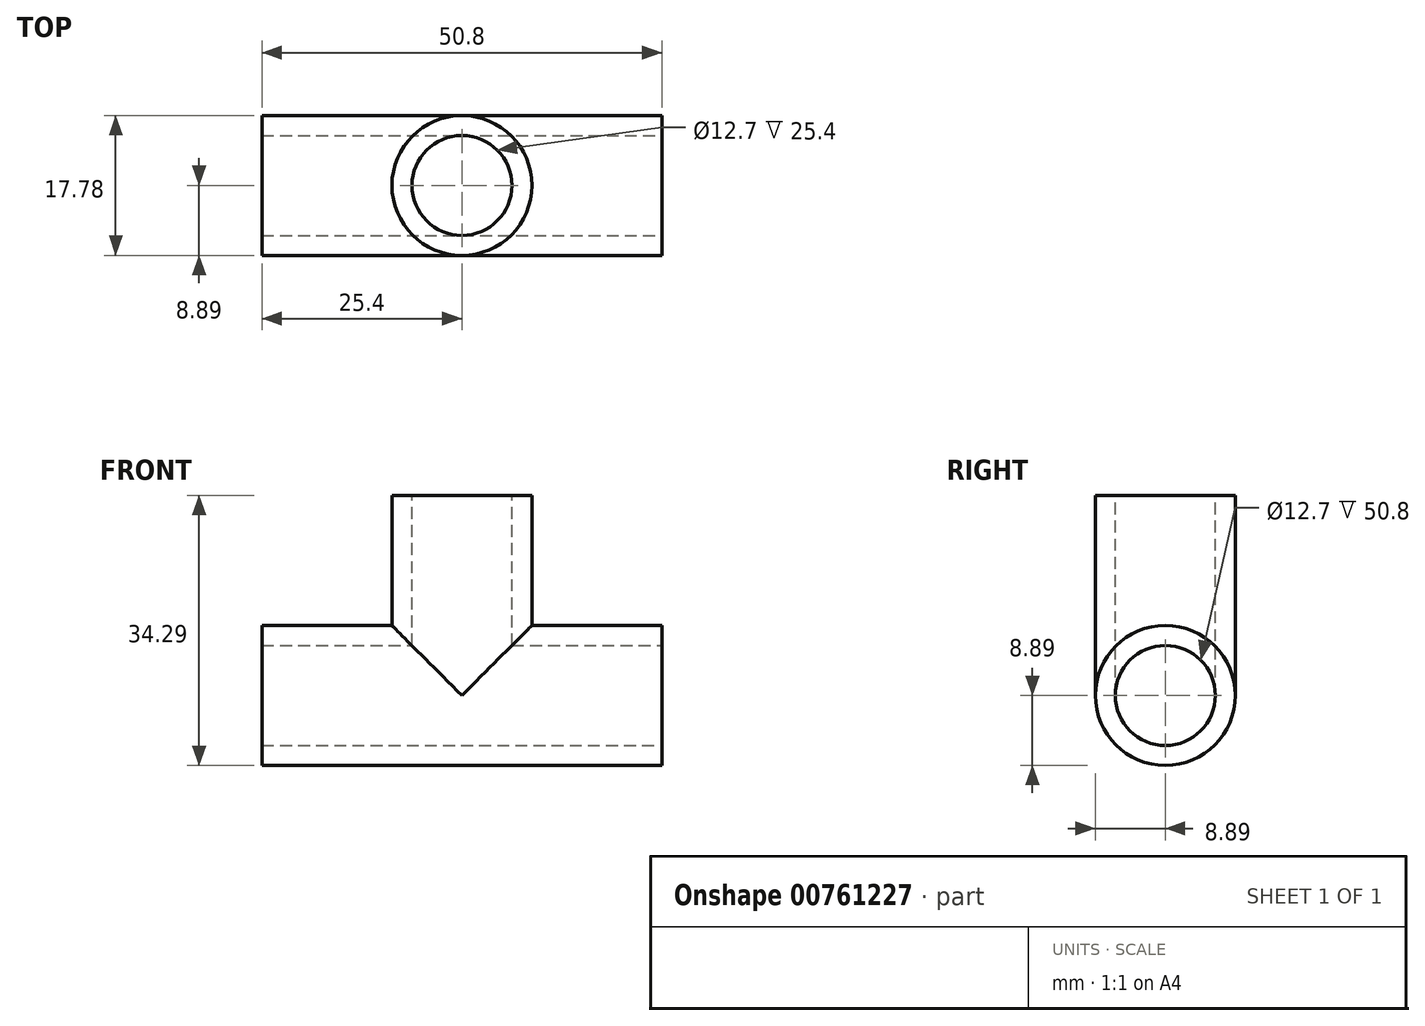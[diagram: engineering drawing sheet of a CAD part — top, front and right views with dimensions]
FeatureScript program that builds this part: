
annotation { "Feature Type Name" : "Feature", "Feature Type Description" : "" }
export const myFeature = defineFeature(function(context is Context, id is Id, definition is map)
    precondition{}
    {
        {
            var Q0;
            Q0=qCreatedBy(makeId("Right.planeOp"),FACE);
            var sketch = newSketch(context, id + "F0", { "sketchPlane" : qUnion([Q0])});
            skLineSegment(sketch, "E0", {"start": v(8.89, 0) * mm, "end": v(8.89, 25.4) * mm});
            skLineSegment(sketch, "E1", {"start": v(8.89, 25.4) * mm, "end": v(0, 25.4) * mm});
            skLineSegment(sketch, "E2", {"start": v(0, 25.4) * mm, "end": v(0, 0) * mm});
            skLineSegment(sketch, "E3", {"start": v(0, 0) * mm, "end": v(8.89, 0) * mm});
            skLineSegment(sketch, "E4", {"start": v(0, 25.4) * mm, "end": v(0, 0) * mm, "construction": true});
            skSolve(sketch);
        }
        {
            var Q0;
            Q0=makeQuery(id+"F0.imprint","IMPRINT",FACE,{"disambiguationData":[TD([[makeQuery(id+"F0.imprint","IMPRINT",EDGE,{"derivedFrom":sQuery(id+"F0.wireOp",EDGE,"E0")}),1.0]])]});
            var Q1;
            Q1=sQuery(id+"F0.wireOp",EDGE,"E4");
            revolve(context, id + "F1", {"surfaceOperationType" : NewSurfaceOperationType.NEW, "entities" : qUnion([Q0]), "axis" : qUnion([Q1]), "revolveType" : RevolveType.FULL});
        }
        {
            var Q0;
            Q0=qCreatedBy(makeId("Top.planeOp"),FACE);
            var sketch = newSketch(context, id + "F2", { "sketchPlane" : qUnion([Q0])});
            skLineSegment(sketch, "E5", {"start": v(0, 0) * mm, "end": v(-25.4, 0) * mm, "construction": true});
            skLineSegment(sketch, "E6", {"start": v(0, 0) * mm, "end": v(25.4, 0) * mm, "construction": true});
            skLineSegment(sketch, "E7", {"start": v(-25.4, 0) * mm, "end": v(-25.4, 8.89) * mm});
            skLineSegment(sketch, "E8", {"start": v(25.4, 8.9) * mm, "end": v(25.4, 0) * mm});
            skLineSegment(sketch, "E9", {"start": v(-25.4, 8.89) * mm, "end": v(25.4, 8.9) * mm});
            skLineSegment(sketch, "E10", {"start": v(25.4, 0) * mm, "end": v(-25.4, 0) * mm});
            skSolve(sketch);
        }
        {
            var Q0;
            Q0=makeQuery(id+"F2.imprint","IMPRINT",FACE,{"disambiguationData":[TD([[makeQuery(id+"F2.imprint","IMPRINT",EDGE,{"derivedFrom":sQuery(id+"F2.wireOp",EDGE,"E7")}),-1.0]])]});
            var Q1;
            Q1=sQuery(id+"F2.wireOp",EDGE,"E5");
            revolve(context, id + "F3", {"operationType" : NewBodyOperationType.ADD, "surfaceOperationType" : NewSurfaceOperationType.NEW, "entities" : qUnion([Q0]), "axis" : qUnion([Q1]), "revolveType" : RevolveType.FULL});
        }
        {
            var Q0;
            Q0=makeQuery(id+"F3.opRevolve","SWEPT_FACE",FACE,{"disambiguationData":[OSD([sQuery(id+"F2.wireOp",EDGE,"E8")])]});
            var Q1;
            Q1=makeQuery(id+"F3.opRevolve","SWEPT_FACE",FACE,{"disambiguationData":[OSD([sQuery(id+"F2.wireOp",EDGE,"E7")])]});
            var Q2;
            Q2=makeQuery(id+"F1.opRevolve","SWEPT_FACE",FACE,{"disambiguationData":[OSD([sQuery(id+"F0.wireOp",EDGE,"E1")])]});
            shell(context, id + "F4", {"entities" : qUnion([Q0, Q1, Q2]), "thickness" : 2.54 * mm});
        }
    });
